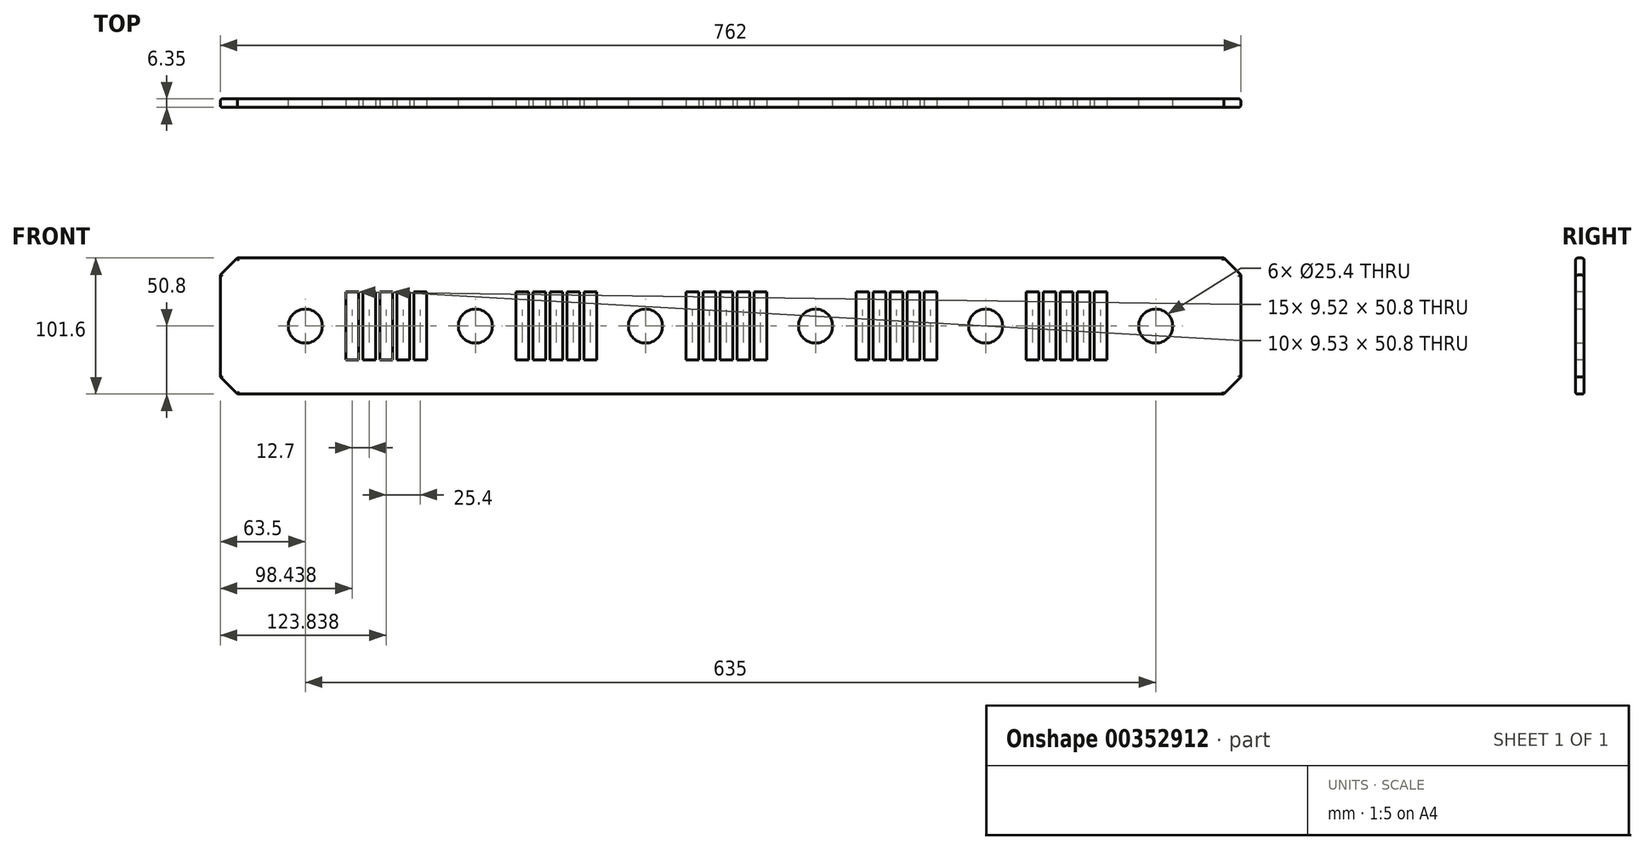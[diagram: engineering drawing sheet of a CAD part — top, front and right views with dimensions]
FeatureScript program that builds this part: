
annotation { "Feature Type Name" : "Feature", "Feature Type Description" : "" }
export const myFeature = defineFeature(function(context is Context, id is Id, definition is map)
    precondition{}
    {
        {
            var Q0;
            Q0=qCreatedBy(makeId("Front.planeOp"),FACE);
            var sketch = newSketch(context, id + "F0", { "sketchPlane" : qUnion([Q0])});
            skLineSegment(sketch, "E0.bottom", {"start": v(0, 0) * mm, "end": v(762, 0) * mm});
            skLineSegment(sketch, "E0.top", {"start": v(0, 101.6) * mm, "end": v(762, 101.6) * mm});
            skLineSegment(sketch, "E0.left", {"start": v(0, 0) * mm, "end": v(0, 101.6) * mm});
            skLineSegment(sketch, "E0.right", {"start": v(762, 0) * mm, "end": v(762, 101.6) * mm});
            skCircle(sketch, "E1", {"center": v(63.5, 50.8) * mm, "radius": 12.7 * mm});
            skPoint(sketch, "E1.centerSnap0", {"position": v(0, 50.8) * mm});
            skCircle(sketch, "E2", {"center": v(190.5, 50.8) * mm, "radius": 12.7 * mm});
            skCircle(sketch, "E3", {"center": v(317.5, 50.8) * mm, "radius": 12.7 * mm});
            skCircle(sketch, "E4", {"center": v(444.5, 50.8) * mm, "radius": 12.7 * mm});
            skCircle(sketch, "E5", {"center": v(571.5, 50.8) * mm, "radius": 12.7 * mm});
            skCircle(sketch, "E6", {"center": v(698.5, 50.8) * mm, "radius": 12.7 * mm});
            skSolve(sketch);
        }
        {
            var Q0;
            Q0=qSketchRegion(id+"F0",true);
            extrude(context, id + "F1", {"entities" : qUnion([Q0]), "depth" : 6.35 * mm});
        }
        {
            var Q0;
            Q0=makeQuery(id+"F1.opExtrude","CAP_FACE",FACE,{"disambiguationData":[OSD([sQuery(id+"F0.wireOp",EDGE,"E0.bottom"),sQuery(id+"F0.wireOp",EDGE,"E0.top"),sQuery(id+"F0.wireOp",EDGE,"E0.left"),sQuery(id+"F0.wireOp",EDGE,"E0.right"),sQuery(id+"F0.wireOp",EDGE,"E1"),sQuery(id+"F0.wireOp",EDGE,"E2"),sQuery(id+"F0.wireOp",EDGE,"E3"),sQuery(id+"F0.wireOp",EDGE,"E4"),sQuery(id+"F0.wireOp",EDGE,"E5"),sQuery(id+"F0.wireOp",EDGE,"E6")])],"isStart":false});
            var sketch = newSketch(context, id + "F2", { "sketchPlane" : qUnion([Q0])});
            skLineSegment(sketch, "E7.bottom", {"start": v(93.68, 76.2) * mm, "end": v(103.2, 76.2) * mm});
            skLineSegment(sketch, "E7.top", {"start": v(93.68, 25.4) * mm, "end": v(103.2, 25.4) * mm});
            skLineSegment(sketch, "E7.left", {"start": v(93.68, 76.2) * mm, "end": v(93.68, 25.4) * mm});
            skLineSegment(sketch, "E7.right", {"start": v(103.2, 76.2) * mm, "end": v(103.2, 25.4) * mm});
            skLineSegment(sketch, "E8.1.0.0", {"start": v(106.38, 76.2) * mm, "end": v(115.9, 76.2) * mm});
            skLineSegment(sketch, "E8.1.0.1", {"start": v(106.38, 25.4) * mm, "end": v(115.9, 25.4) * mm});
            skLineSegment(sketch, "E8.1.0.2", {"start": v(106.38, 76.2) * mm, "end": v(106.38, 25.4) * mm});
            skLineSegment(sketch, "E8.1.0.3", {"start": v(115.9, 76.2) * mm, "end": v(115.9, 25.4) * mm});
            skLineSegment(sketch, "E8.2.0.0", {"start": v(119.08, 76.2) * mm, "end": v(128.6, 76.2) * mm});
            skLineSegment(sketch, "E8.2.0.1", {"start": v(119.08, 25.4) * mm, "end": v(128.6, 25.4) * mm});
            skLineSegment(sketch, "E8.2.0.2", {"start": v(119.08, 76.2) * mm, "end": v(119.08, 25.4) * mm});
            skLineSegment(sketch, "E8.2.0.3", {"start": v(128.6, 76.2) * mm, "end": v(128.6, 25.4) * mm});
            skLineSegment(sketch, "E8.3.0.0", {"start": v(131.78, 76.2) * mm, "end": v(141.3, 76.2) * mm});
            skLineSegment(sketch, "E8.3.0.1", {"start": v(131.78, 25.4) * mm, "end": v(141.3, 25.4) * mm});
            skLineSegment(sketch, "E8.3.0.2", {"start": v(131.78, 76.2) * mm, "end": v(131.78, 25.4) * mm});
            skLineSegment(sketch, "E8.3.0.3", {"start": v(141.3, 76.2) * mm, "end": v(141.3, 25.4) * mm});
            skLineSegment(sketch, "E8.4.0.0", {"start": v(144.48, 76.2) * mm, "end": v(154, 76.2) * mm});
            skLineSegment(sketch, "E8.4.0.1", {"start": v(144.48, 25.4) * mm, "end": v(154, 25.4) * mm});
            skLineSegment(sketch, "E8.4.0.2", {"start": v(144.48, 76.2) * mm, "end": v(144.48, 25.4) * mm});
            skLineSegment(sketch, "E8.4.0.3", {"start": v(154, 76.2) * mm, "end": v(154, 25.4) * mm});
            skLineSegment(sketch, "E8.direction1", {"start": v(93.68, 76.2) * mm, "end": v(106.38, 76.2) * mm, "construction": true});
            skLineSegment(sketch, "E9.bottom", {"start": v(220.68, 76.2) * mm, "end": v(230.2, 76.2) * mm});
            skLineSegment(sketch, "E9.top", {"start": v(220.68, 25.4) * mm, "end": v(230.2, 25.4) * mm});
            skLineSegment(sketch, "E9.left", {"start": v(220.68, 76.2) * mm, "end": v(220.68, 25.4) * mm});
            skLineSegment(sketch, "E9.right", {"start": v(230.2, 76.2) * mm, "end": v(230.2, 25.4) * mm});
            skLineSegment(sketch, "E10.1.0.0", {"start": v(233.38, 76.2) * mm, "end": v(233.38, 25.4) * mm});
            skLineSegment(sketch, "E10.1.0.1", {"start": v(242.9, 76.2) * mm, "end": v(242.9, 25.4) * mm});
            skLineSegment(sketch, "E10.1.0.2", {"start": v(233.38, 76.2) * mm, "end": v(242.9, 76.2) * mm});
            skLineSegment(sketch, "E10.1.0.3", {"start": v(233.38, 25.4) * mm, "end": v(242.9, 25.4) * mm});
            skLineSegment(sketch, "E10.2.0.0", {"start": v(246.08, 76.2) * mm, "end": v(246.08, 25.4) * mm});
            skLineSegment(sketch, "E10.2.0.1", {"start": v(255.6, 76.2) * mm, "end": v(255.6, 25.4) * mm});
            skLineSegment(sketch, "E10.2.0.2", {"start": v(246.08, 76.2) * mm, "end": v(255.6, 76.2) * mm});
            skLineSegment(sketch, "E10.2.0.3", {"start": v(246.08, 25.4) * mm, "end": v(255.6, 25.4) * mm});
            skLineSegment(sketch, "E10.3.0.0", {"start": v(258.78, 76.2) * mm, "end": v(258.78, 25.4) * mm});
            skLineSegment(sketch, "E10.3.0.1", {"start": v(268.3, 76.2) * mm, "end": v(268.3, 25.4) * mm});
            skLineSegment(sketch, "E10.3.0.2", {"start": v(258.78, 76.2) * mm, "end": v(268.3, 76.2) * mm});
            skLineSegment(sketch, "E10.3.0.3", {"start": v(258.78, 25.4) * mm, "end": v(268.3, 25.4) * mm});
            skLineSegment(sketch, "E10.4.0.0", {"start": v(271.48, 76.2) * mm, "end": v(271.48, 25.4) * mm});
            skLineSegment(sketch, "E10.4.0.1", {"start": v(281, 76.2) * mm, "end": v(281, 25.4) * mm});
            skLineSegment(sketch, "E10.4.0.2", {"start": v(271.48, 76.2) * mm, "end": v(281, 76.2) * mm});
            skLineSegment(sketch, "E10.4.0.3", {"start": v(271.48, 25.4) * mm, "end": v(281, 25.4) * mm});
            skLineSegment(sketch, "E10.direction1", {"start": v(220.68, 25.4) * mm, "end": v(233.38, 25.4) * mm, "construction": true});
            skLineSegment(sketch, "E11.bottom", {"start": v(347.68, 76.2) * mm, "end": v(357.2, 76.2) * mm});
            skLineSegment(sketch, "E11.top", {"start": v(347.68, 25.4) * mm, "end": v(357.2, 25.4) * mm});
            skLineSegment(sketch, "E11.left", {"start": v(347.68, 76.2) * mm, "end": v(347.68, 25.4) * mm});
            skLineSegment(sketch, "E11.right", {"start": v(357.2, 76.2) * mm, "end": v(357.2, 25.4) * mm});
            skLineSegment(sketch, "E12.1.0.0", {"start": v(360.38, 76.2) * mm, "end": v(369.9, 76.2) * mm});
            skLineSegment(sketch, "E12.1.0.1", {"start": v(360.38, 25.4) * mm, "end": v(369.9, 25.4) * mm});
            skLineSegment(sketch, "E12.1.0.2", {"start": v(360.38, 76.2) * mm, "end": v(360.38, 25.4) * mm});
            skLineSegment(sketch, "E12.1.0.3", {"start": v(369.9, 76.2) * mm, "end": v(369.9, 25.4) * mm});
            skLineSegment(sketch, "E12.2.0.0", {"start": v(373.08, 76.2) * mm, "end": v(382.6, 76.2) * mm});
            skLineSegment(sketch, "E12.2.0.1", {"start": v(373.08, 25.4) * mm, "end": v(382.6, 25.4) * mm});
            skLineSegment(sketch, "E12.2.0.2", {"start": v(373.08, 76.2) * mm, "end": v(373.08, 25.4) * mm});
            skLineSegment(sketch, "E12.2.0.3", {"start": v(382.6, 76.2) * mm, "end": v(382.6, 25.4) * mm});
            skLineSegment(sketch, "E12.3.0.0", {"start": v(385.78, 76.2) * mm, "end": v(395.3, 76.2) * mm});
            skLineSegment(sketch, "E12.3.0.1", {"start": v(385.78, 25.4) * mm, "end": v(395.3, 25.4) * mm});
            skLineSegment(sketch, "E12.3.0.2", {"start": v(385.78, 76.2) * mm, "end": v(385.78, 25.4) * mm});
            skLineSegment(sketch, "E12.3.0.3", {"start": v(395.3, 76.2) * mm, "end": v(395.3, 25.4) * mm});
            skLineSegment(sketch, "E12.4.0.0", {"start": v(398.48, 76.2) * mm, "end": v(408, 76.2) * mm});
            skLineSegment(sketch, "E12.4.0.1", {"start": v(398.48, 25.4) * mm, "end": v(408, 25.4) * mm});
            skLineSegment(sketch, "E12.4.0.2", {"start": v(398.48, 76.2) * mm, "end": v(398.48, 25.4) * mm});
            skLineSegment(sketch, "E12.4.0.3", {"start": v(408, 76.2) * mm, "end": v(408, 25.4) * mm});
            skLineSegment(sketch, "E12.direction1", {"start": v(347.68, 76.2) * mm, "end": v(360.38, 76.2) * mm, "construction": true});
            skLineSegment(sketch, "E13.bottom", {"start": v(474.68, 76.2) * mm, "end": v(484.2, 76.2) * mm});
            skLineSegment(sketch, "E13.top", {"start": v(474.68, 25.4) * mm, "end": v(484.2, 25.4) * mm});
            skLineSegment(sketch, "E13.left", {"start": v(474.68, 76.2) * mm, "end": v(474.68, 25.4) * mm});
            skLineSegment(sketch, "E13.right", {"start": v(484.2, 76.2) * mm, "end": v(484.2, 25.4) * mm});
            skLineSegment(sketch, "E14.1.0.0", {"start": v(487.38, 76.2) * mm, "end": v(487.38, 25.4) * mm});
            skLineSegment(sketch, "E14.1.0.1", {"start": v(496.9, 76.2) * mm, "end": v(496.9, 25.4) * mm});
            skLineSegment(sketch, "E14.1.0.2", {"start": v(487.38, 76.2) * mm, "end": v(496.9, 76.2) * mm});
            skLineSegment(sketch, "E14.1.0.3", {"start": v(487.38, 25.4) * mm, "end": v(496.9, 25.4) * mm});
            skLineSegment(sketch, "E14.2.0.0", {"start": v(500.08, 76.2) * mm, "end": v(500.08, 25.4) * mm});
            skLineSegment(sketch, "E14.2.0.1", {"start": v(509.6, 76.2) * mm, "end": v(509.6, 25.4) * mm});
            skLineSegment(sketch, "E14.2.0.2", {"start": v(500.08, 76.2) * mm, "end": v(509.6, 76.2) * mm});
            skLineSegment(sketch, "E14.2.0.3", {"start": v(500.08, 25.4) * mm, "end": v(509.6, 25.4) * mm});
            skLineSegment(sketch, "E14.3.0.0", {"start": v(512.78, 76.2) * mm, "end": v(512.78, 25.4) * mm});
            skLineSegment(sketch, "E14.3.0.1", {"start": v(522.3, 76.2) * mm, "end": v(522.3, 25.4) * mm});
            skLineSegment(sketch, "E14.3.0.2", {"start": v(512.78, 76.2) * mm, "end": v(522.3, 76.2) * mm});
            skLineSegment(sketch, "E14.3.0.3", {"start": v(512.78, 25.4) * mm, "end": v(522.3, 25.4) * mm});
            skLineSegment(sketch, "E14.4.0.0", {"start": v(525.48, 76.2) * mm, "end": v(525.48, 25.4) * mm});
            skLineSegment(sketch, "E14.4.0.1", {"start": v(535, 76.2) * mm, "end": v(535, 25.4) * mm});
            skLineSegment(sketch, "E14.4.0.2", {"start": v(525.48, 76.2) * mm, "end": v(535, 76.2) * mm});
            skLineSegment(sketch, "E14.4.0.3", {"start": v(525.48, 25.4) * mm, "end": v(535, 25.4) * mm});
            skLineSegment(sketch, "E14.direction1", {"start": v(474.68, 25.4) * mm, "end": v(487.38, 25.4) * mm, "construction": true});
            skLineSegment(sketch, "E15.bottom", {"start": v(601.68, 76.2) * mm, "end": v(611.2, 76.2) * mm});
            skLineSegment(sketch, "E15.top", {"start": v(601.68, 25.4) * mm, "end": v(611.2, 25.4) * mm});
            skLineSegment(sketch, "E15.left", {"start": v(601.68, 76.2) * mm, "end": v(601.68, 25.4) * mm});
            skLineSegment(sketch, "E15.right", {"start": v(611.2, 76.2) * mm, "end": v(611.2, 25.4) * mm});
            skLineSegment(sketch, "E16.1.0.0", {"start": v(614.38, 76.2) * mm, "end": v(623.9, 76.2) * mm});
            skLineSegment(sketch, "E16.1.0.1", {"start": v(614.38, 76.2) * mm, "end": v(614.38, 25.4) * mm});
            skLineSegment(sketch, "E16.1.0.2", {"start": v(623.9, 76.2) * mm, "end": v(623.9, 25.4) * mm});
            skLineSegment(sketch, "E16.1.0.3", {"start": v(614.38, 25.4) * mm, "end": v(623.9, 25.4) * mm});
            skLineSegment(sketch, "E16.2.0.0", {"start": v(627.08, 76.2) * mm, "end": v(636.6, 76.2) * mm});
            skLineSegment(sketch, "E16.2.0.1", {"start": v(627.08, 76.2) * mm, "end": v(627.08, 25.4) * mm});
            skLineSegment(sketch, "E16.2.0.2", {"start": v(636.6, 76.2) * mm, "end": v(636.6, 25.4) * mm});
            skLineSegment(sketch, "E16.2.0.3", {"start": v(627.08, 25.4) * mm, "end": v(636.6, 25.4) * mm});
            skLineSegment(sketch, "E16.3.0.0", {"start": v(639.78, 76.2) * mm, "end": v(649.3, 76.2) * mm});
            skLineSegment(sketch, "E16.3.0.1", {"start": v(639.78, 76.2) * mm, "end": v(639.78, 25.4) * mm});
            skLineSegment(sketch, "E16.3.0.2", {"start": v(649.3, 76.2) * mm, "end": v(649.3, 25.4) * mm});
            skLineSegment(sketch, "E16.3.0.3", {"start": v(639.78, 25.4) * mm, "end": v(649.3, 25.4) * mm});
            skLineSegment(sketch, "E16.4.0.0", {"start": v(652.48, 76.2) * mm, "end": v(662, 76.2) * mm});
            skLineSegment(sketch, "E16.4.0.1", {"start": v(652.48, 76.2) * mm, "end": v(652.48, 25.4) * mm});
            skLineSegment(sketch, "E16.4.0.2", {"start": v(662, 76.2) * mm, "end": v(662, 25.4) * mm});
            skLineSegment(sketch, "E16.4.0.3", {"start": v(652.48, 25.4) * mm, "end": v(662, 25.4) * mm});
            skLineSegment(sketch, "E16.direction1", {"start": v(601.68, 76.2) * mm, "end": v(614.38, 76.2) * mm, "construction": true});
            skSolve(sketch);
        }
        {
            var Q0;
            Q0=qSketchRegion(id+"F2",true);
            extrude(context, id + "F3", {"entities" : qUnion([Q0]), "operationType" : NewBodyOperationType.REMOVE, "endBound" : BoundingType.THROUGH_ALL, "oppositeDirection" : true, "depth" : 25.4 * mm});
        }
        {
            var Q0;
            Q0=makeQuery(id+"F1.opExtrude","SWEPT_EDGE",EDGE,{"disambiguationData":[OSD([sQuery(id+"F0.wireOp",EDGE,"E0.top"),sQuery(id+"F0.wireOp",EDGE,"E0.left")])]});
            var Q1;
            Q1=makeQuery(id+"F1.opExtrude","SWEPT_EDGE",EDGE,{"disambiguationData":[OSD([sQuery(id+"F0.wireOp",EDGE,"E0.bottom"),sQuery(id+"F0.wireOp",EDGE,"E0.left")])]});
            var Q2;
            Q2=makeQuery(id+"F1.opExtrude","SWEPT_EDGE",EDGE,{"disambiguationData":[OSD([sQuery(id+"F0.wireOp",EDGE,"E0.top"),sQuery(id+"F0.wireOp",EDGE,"E0.right")])]});
            var Q3;
            Q3=makeQuery(id+"F1.opExtrude","SWEPT_EDGE",EDGE,{"disambiguationData":[OSD([sQuery(id+"F0.wireOp",EDGE,"E0.bottom"),sQuery(id+"F0.wireOp",EDGE,"E0.right")])]});
            chamfer(context, id + "F4", {"entities" : qUnion([Q0, Q1, Q2, Q3]), "width" : 12.7 * mm, "tangentPropagation" : true});
        }
        {
            var Q0;
            Q0=makeQuery(id+"F1.opExtrude","CAP_EDGE",EDGE,{"disambiguationData":[OSD([sQuery(id+"F0.wireOp",EDGE,"E0.top")])],"isStart":false});
            var Q1;
            Q1=makeQuery(id+"F1.opExtrude","CAP_EDGE",EDGE,{"disambiguationData":[OSD([sQuery(id+"F0.wireOp",EDGE,"E0.top")])],"isStart":true});
            var Q2;
            Q2=makeQuery(id+"F1.opExtrude","CAP_EDGE",EDGE,{"disambiguationData":[OSD([sQuery(id+"F0.wireOp",EDGE,"E0.bottom")])],"isStart":false});
            var Q3;
            Q3=makeQuery(id+"F1.opExtrude","CAP_EDGE",EDGE,{"disambiguationData":[OSD([sQuery(id+"F0.wireOp",EDGE,"E0.bottom")])],"isStart":true});
            var Q4;
            {var subQ0=sQuery(id+"F0.wireOp",EDGE,"E0.left");var subQ1=sQuery(id+"F0.wireOp",EDGE,"E0.top");Q4=makeQuery(id+"F4.opChamfer","BLEND_EDGE",EDGE,{"blendedFrom":[makeQuery(id+"F1.opExtrude","SWEPT_EDGE",EDGE,{"disambiguationData":[OSD([subQ1,subQ0])]}),makeQuery(id+"F1.opExtrude","CAP_FACE",FACE,{"disambiguationData":[OSD([sQuery(id+"F0.wireOp",EDGE,"E0.bottom"),subQ1,subQ0,sQuery(id+"F0.wireOp",EDGE,"E0.right"),sQuery(id+"F0.wireOp",EDGE,"E1"),sQuery(id+"F0.wireOp",EDGE,"E2"),sQuery(id+"F0.wireOp",EDGE,"E3"),sQuery(id+"F0.wireOp",EDGE,"E4"),sQuery(id+"F0.wireOp",EDGE,"E5"),sQuery(id+"F0.wireOp",EDGE,"E6")])],"isStart":false})],"blendedInto":[makeQuery(id+"F1.opExtrude","CAP_FACE",FACE,{"disambiguationData":[OSD([sQuery(id+"F0.wireOp",EDGE,"E0.bottom"),subQ1,subQ0,sQuery(id+"F0.wireOp",EDGE,"E0.right"),sQuery(id+"F0.wireOp",EDGE,"E1"),sQuery(id+"F0.wireOp",EDGE,"E2"),sQuery(id+"F0.wireOp",EDGE,"E3"),sQuery(id+"F0.wireOp",EDGE,"E4"),sQuery(id+"F0.wireOp",EDGE,"E5"),sQuery(id+"F0.wireOp",EDGE,"E6")])],"isStart":false})]});}
            var Q5;
            {var subQ0=sQuery(id+"F0.wireOp",EDGE,"E0.left");var subQ1=sQuery(id+"F0.wireOp",EDGE,"E0.top");Q5=makeQuery(id+"F4.opChamfer","BLEND_EDGE",EDGE,{"blendedFrom":[makeQuery(id+"F1.opExtrude","SWEPT_EDGE",EDGE,{"disambiguationData":[OSD([subQ1,subQ0])]}),makeQuery(id+"F1.opExtrude","CAP_FACE",FACE,{"disambiguationData":[OSD([sQuery(id+"F0.wireOp",EDGE,"E0.bottom"),subQ1,subQ0,sQuery(id+"F0.wireOp",EDGE,"E0.right"),sQuery(id+"F0.wireOp",EDGE,"E1"),sQuery(id+"F0.wireOp",EDGE,"E2"),sQuery(id+"F0.wireOp",EDGE,"E3"),sQuery(id+"F0.wireOp",EDGE,"E4"),sQuery(id+"F0.wireOp",EDGE,"E5"),sQuery(id+"F0.wireOp",EDGE,"E6")])],"isStart":true})],"blendedInto":[makeQuery(id+"F1.opExtrude","CAP_FACE",FACE,{"disambiguationData":[OSD([sQuery(id+"F0.wireOp",EDGE,"E0.bottom"),subQ1,subQ0,sQuery(id+"F0.wireOp",EDGE,"E0.right"),sQuery(id+"F0.wireOp",EDGE,"E1"),sQuery(id+"F0.wireOp",EDGE,"E2"),sQuery(id+"F0.wireOp",EDGE,"E3"),sQuery(id+"F0.wireOp",EDGE,"E4"),sQuery(id+"F0.wireOp",EDGE,"E5"),sQuery(id+"F0.wireOp",EDGE,"E6")])],"isStart":true})]});}
            var Q6;
            Q6=makeQuery(id+"F1.opExtrude","CAP_EDGE",EDGE,{"disambiguationData":[OSD([sQuery(id+"F0.wireOp",EDGE,"E0.left")])],"isStart":false});
            var Q7;
            Q7=makeQuery(id+"F1.opExtrude","CAP_EDGE",EDGE,{"disambiguationData":[OSD([sQuery(id+"F0.wireOp",EDGE,"E0.left")])],"isStart":true});
            var Q8;
            {var subQ0=sQuery(id+"F0.wireOp",EDGE,"E0.left");var subQ1=sQuery(id+"F0.wireOp",EDGE,"E0.bottom");Q8=makeQuery(id+"F4.opChamfer","BLEND_EDGE",EDGE,{"blendedFrom":[makeQuery(id+"F1.opExtrude","SWEPT_EDGE",EDGE,{"disambiguationData":[OSD([subQ1,subQ0])]}),makeQuery(id+"F1.opExtrude","CAP_FACE",FACE,{"disambiguationData":[OSD([subQ1,sQuery(id+"F0.wireOp",EDGE,"E0.top"),subQ0,sQuery(id+"F0.wireOp",EDGE,"E0.right"),sQuery(id+"F0.wireOp",EDGE,"E1"),sQuery(id+"F0.wireOp",EDGE,"E2"),sQuery(id+"F0.wireOp",EDGE,"E3"),sQuery(id+"F0.wireOp",EDGE,"E4"),sQuery(id+"F0.wireOp",EDGE,"E5"),sQuery(id+"F0.wireOp",EDGE,"E6")])],"isStart":false})],"blendedInto":[makeQuery(id+"F1.opExtrude","CAP_FACE",FACE,{"disambiguationData":[OSD([subQ1,sQuery(id+"F0.wireOp",EDGE,"E0.top"),subQ0,sQuery(id+"F0.wireOp",EDGE,"E0.right"),sQuery(id+"F0.wireOp",EDGE,"E1"),sQuery(id+"F0.wireOp",EDGE,"E2"),sQuery(id+"F0.wireOp",EDGE,"E3"),sQuery(id+"F0.wireOp",EDGE,"E4"),sQuery(id+"F0.wireOp",EDGE,"E5"),sQuery(id+"F0.wireOp",EDGE,"E6")])],"isStart":false})]});}
            var Q9;
            {var subQ0=sQuery(id+"F0.wireOp",EDGE,"E0.left");var subQ1=sQuery(id+"F0.wireOp",EDGE,"E0.bottom");Q9=makeQuery(id+"F4.opChamfer","BLEND_EDGE",EDGE,{"blendedFrom":[makeQuery(id+"F1.opExtrude","SWEPT_EDGE",EDGE,{"disambiguationData":[OSD([subQ1,subQ0])]}),makeQuery(id+"F1.opExtrude","CAP_FACE",FACE,{"disambiguationData":[OSD([subQ1,sQuery(id+"F0.wireOp",EDGE,"E0.top"),subQ0,sQuery(id+"F0.wireOp",EDGE,"E0.right"),sQuery(id+"F0.wireOp",EDGE,"E1"),sQuery(id+"F0.wireOp",EDGE,"E2"),sQuery(id+"F0.wireOp",EDGE,"E3"),sQuery(id+"F0.wireOp",EDGE,"E4"),sQuery(id+"F0.wireOp",EDGE,"E5"),sQuery(id+"F0.wireOp",EDGE,"E6")])],"isStart":true})],"blendedInto":[makeQuery(id+"F1.opExtrude","CAP_FACE",FACE,{"disambiguationData":[OSD([subQ1,sQuery(id+"F0.wireOp",EDGE,"E0.top"),subQ0,sQuery(id+"F0.wireOp",EDGE,"E0.right"),sQuery(id+"F0.wireOp",EDGE,"E1"),sQuery(id+"F0.wireOp",EDGE,"E2"),sQuery(id+"F0.wireOp",EDGE,"E3"),sQuery(id+"F0.wireOp",EDGE,"E4"),sQuery(id+"F0.wireOp",EDGE,"E5"),sQuery(id+"F0.wireOp",EDGE,"E6")])],"isStart":true})]});}
            var Q10;
            {var subQ0=sQuery(id+"F0.wireOp",EDGE,"E0.right");var subQ1=sQuery(id+"F0.wireOp",EDGE,"E0.top");Q10=makeQuery(id+"F4.opChamfer","BLEND_EDGE",EDGE,{"blendedFrom":[makeQuery(id+"F1.opExtrude","SWEPT_EDGE",EDGE,{"disambiguationData":[OSD([subQ1,subQ0])]}),makeQuery(id+"F1.opExtrude","CAP_FACE",FACE,{"disambiguationData":[OSD([sQuery(id+"F0.wireOp",EDGE,"E0.bottom"),subQ1,sQuery(id+"F0.wireOp",EDGE,"E0.left"),subQ0,sQuery(id+"F0.wireOp",EDGE,"E1"),sQuery(id+"F0.wireOp",EDGE,"E2"),sQuery(id+"F0.wireOp",EDGE,"E3"),sQuery(id+"F0.wireOp",EDGE,"E4"),sQuery(id+"F0.wireOp",EDGE,"E5"),sQuery(id+"F0.wireOp",EDGE,"E6")])],"isStart":false})],"blendedInto":[makeQuery(id+"F1.opExtrude","CAP_FACE",FACE,{"disambiguationData":[OSD([sQuery(id+"F0.wireOp",EDGE,"E0.bottom"),subQ1,sQuery(id+"F0.wireOp",EDGE,"E0.left"),subQ0,sQuery(id+"F0.wireOp",EDGE,"E1"),sQuery(id+"F0.wireOp",EDGE,"E2"),sQuery(id+"F0.wireOp",EDGE,"E3"),sQuery(id+"F0.wireOp",EDGE,"E4"),sQuery(id+"F0.wireOp",EDGE,"E5"),sQuery(id+"F0.wireOp",EDGE,"E6")])],"isStart":false})]});}
            var Q11;
            {var subQ0=sQuery(id+"F0.wireOp",EDGE,"E0.right");var subQ1=sQuery(id+"F0.wireOp",EDGE,"E0.top");Q11=makeQuery(id+"F4.opChamfer","BLEND_EDGE",EDGE,{"blendedFrom":[makeQuery(id+"F1.opExtrude","SWEPT_EDGE",EDGE,{"disambiguationData":[OSD([subQ1,subQ0])]}),makeQuery(id+"F1.opExtrude","CAP_FACE",FACE,{"disambiguationData":[OSD([sQuery(id+"F0.wireOp",EDGE,"E0.bottom"),subQ1,sQuery(id+"F0.wireOp",EDGE,"E0.left"),subQ0,sQuery(id+"F0.wireOp",EDGE,"E1"),sQuery(id+"F0.wireOp",EDGE,"E2"),sQuery(id+"F0.wireOp",EDGE,"E3"),sQuery(id+"F0.wireOp",EDGE,"E4"),sQuery(id+"F0.wireOp",EDGE,"E5"),sQuery(id+"F0.wireOp",EDGE,"E6")])],"isStart":true})],"blendedInto":[makeQuery(id+"F1.opExtrude","CAP_FACE",FACE,{"disambiguationData":[OSD([sQuery(id+"F0.wireOp",EDGE,"E0.bottom"),subQ1,sQuery(id+"F0.wireOp",EDGE,"E0.left"),subQ0,sQuery(id+"F0.wireOp",EDGE,"E1"),sQuery(id+"F0.wireOp",EDGE,"E2"),sQuery(id+"F0.wireOp",EDGE,"E3"),sQuery(id+"F0.wireOp",EDGE,"E4"),sQuery(id+"F0.wireOp",EDGE,"E5"),sQuery(id+"F0.wireOp",EDGE,"E6")])],"isStart":true})]});}
            var Q12;
            Q12=makeQuery(id+"F1.opExtrude","CAP_EDGE",EDGE,{"disambiguationData":[OSD([sQuery(id+"F0.wireOp",EDGE,"E0.right")])],"isStart":false});
            var Q13;
            Q13=makeQuery(id+"F1.opExtrude","CAP_EDGE",EDGE,{"disambiguationData":[OSD([sQuery(id+"F0.wireOp",EDGE,"E0.right")])],"isStart":true});
            var Q14;
            {var subQ0=sQuery(id+"F0.wireOp",EDGE,"E0.right");var subQ1=sQuery(id+"F0.wireOp",EDGE,"E0.bottom");Q14=makeQuery(id+"F4.opChamfer","BLEND_EDGE",EDGE,{"blendedFrom":[makeQuery(id+"F1.opExtrude","SWEPT_EDGE",EDGE,{"disambiguationData":[OSD([subQ1,subQ0])]}),makeQuery(id+"F1.opExtrude","CAP_FACE",FACE,{"disambiguationData":[OSD([subQ1,sQuery(id+"F0.wireOp",EDGE,"E0.top"),sQuery(id+"F0.wireOp",EDGE,"E0.left"),subQ0,sQuery(id+"F0.wireOp",EDGE,"E1"),sQuery(id+"F0.wireOp",EDGE,"E2"),sQuery(id+"F0.wireOp",EDGE,"E3"),sQuery(id+"F0.wireOp",EDGE,"E4"),sQuery(id+"F0.wireOp",EDGE,"E5"),sQuery(id+"F0.wireOp",EDGE,"E6")])],"isStart":false})],"blendedInto":[makeQuery(id+"F1.opExtrude","CAP_FACE",FACE,{"disambiguationData":[OSD([subQ1,sQuery(id+"F0.wireOp",EDGE,"E0.top"),sQuery(id+"F0.wireOp",EDGE,"E0.left"),subQ0,sQuery(id+"F0.wireOp",EDGE,"E1"),sQuery(id+"F0.wireOp",EDGE,"E2"),sQuery(id+"F0.wireOp",EDGE,"E3"),sQuery(id+"F0.wireOp",EDGE,"E4"),sQuery(id+"F0.wireOp",EDGE,"E5"),sQuery(id+"F0.wireOp",EDGE,"E6")])],"isStart":false})]});}
            var Q15;
            {var subQ0=sQuery(id+"F0.wireOp",EDGE,"E0.right");var subQ1=sQuery(id+"F0.wireOp",EDGE,"E0.bottom");Q15=makeQuery(id+"F4.opChamfer","BLEND_EDGE",EDGE,{"blendedFrom":[makeQuery(id+"F1.opExtrude","SWEPT_EDGE",EDGE,{"disambiguationData":[OSD([subQ1,subQ0])]}),makeQuery(id+"F1.opExtrude","CAP_FACE",FACE,{"disambiguationData":[OSD([subQ1,sQuery(id+"F0.wireOp",EDGE,"E0.top"),sQuery(id+"F0.wireOp",EDGE,"E0.left"),subQ0,sQuery(id+"F0.wireOp",EDGE,"E1"),sQuery(id+"F0.wireOp",EDGE,"E2"),sQuery(id+"F0.wireOp",EDGE,"E3"),sQuery(id+"F0.wireOp",EDGE,"E4"),sQuery(id+"F0.wireOp",EDGE,"E5"),sQuery(id+"F0.wireOp",EDGE,"E6")])],"isStart":true})],"blendedInto":[makeQuery(id+"F1.opExtrude","CAP_FACE",FACE,{"disambiguationData":[OSD([subQ1,sQuery(id+"F0.wireOp",EDGE,"E0.top"),sQuery(id+"F0.wireOp",EDGE,"E0.left"),subQ0,sQuery(id+"F0.wireOp",EDGE,"E1"),sQuery(id+"F0.wireOp",EDGE,"E2"),sQuery(id+"F0.wireOp",EDGE,"E3"),sQuery(id+"F0.wireOp",EDGE,"E4"),sQuery(id+"F0.wireOp",EDGE,"E5"),sQuery(id+"F0.wireOp",EDGE,"E6")])],"isStart":true})]});}
            fillet(context, id + "F5", {"entities" : qUnion([Q0, Q1, Q2, Q3, Q4, Q5, Q6, Q7, Q8, Q9, Q10, Q11, Q12, Q13, Q14, Q15]), "radius" : 1.6 * mm, "tangentPropagation" : true, "allowEdgeOverflow" : false});
        }
    });
